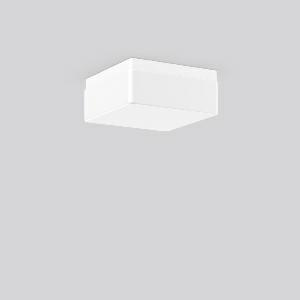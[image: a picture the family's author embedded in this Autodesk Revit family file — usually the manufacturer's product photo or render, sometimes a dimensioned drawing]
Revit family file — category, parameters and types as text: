
# Revit family: quadrat_21129_002_02c3
name_source: partatom
category: Lighting Fixtures
units: mm (PartAtom-declared; Revit-internal decimal feet)

## family parameters
Cut with Voids When Loaded = No
Host = Face
Light Source = No
Part Type = Normal
Room Calculation Point = No
Round Connector Dimension = Use Diameter
Shared = No

## types (1)
- QUADRAT (2 x QA60/clear E27, 700 lm, 46 W, 3000)
    Apparent Load = 92 VA
    CIE Flux Codes = 35 64 86 74 50
    Color Rendering = 90
    Color Temperature = 3000
    Default Elevation = 1800 mm
    Description = Series: QUADRAT
Square surface-mounted luminaire in classic design. Base: plastic. Opal glass: mouth-blown, satin finish. Diffuser fastening: spring system. Suitable for Ceiling mounting, Wall (surface). IP 43 ceiling mounting, IP 44 wall mounting. 
Colour: white
Length: 280 mm
Width: 280 mm
Height: 120 mm
Lamp: A60
Number of lamps: 2
Wattage: 60 W
Socket: E27
System power: 60 W
Rated luminous flux: 370 lm
Luminous efficiency: 6 lm/W
Control gear: Converter not necessary
Protection class: II
Type of protection: IP 43
    Height = 120 mm
    Lamp = 2 x QA60/clear E27
    Lamp Light Flux = 700 lm
    Lamp Power = 46 W
    Lamp count = 2
    Length = 280 mm
    Lifetime = 3000 h
    Luminous efficacy = 8 lm/W
    Manufacturer = RZB
    ModVariant = No
    Model = 21129.002
    Mounting Place = Ceiling, Wall
    Mounting Type = Surface mounted
    Number of Poles = 1
    OnlyDefault = Yes
    Power Factor = 1
    Product Name = QUADRAT
    Product group = Surface mounted ceiling and wall luminaires
    ProductGroupID = 305
    Protection Class = Protection class II
    Protection Degree = IP 43
    RLX_Detail_Level = 1
    RLX_Emergency_Light_Flux = 0 lm
    RLX_Emergency_Type = 0
    RLX_Emergency_Type_DB = No
    RlxData = <blob elided: 11205 chars, md5=3069d5d2>
    Socket = E27
    Standby Power = 0 W
    System Light Flux = 704 lm
    System Power = 92 W
    Type Comments = Product without accessories
    Type Image = 21129.002.jpg
    URL = http://relux.com
    VarID = ---
    Voltage = 230 V
    Voltage Range = 220-240 V
    Weight = 0.00 kg
    Width = 280 mm

## geometry (parser evidence)
native form markers: Sweep x12
no freeform markers — native parametric forms only
